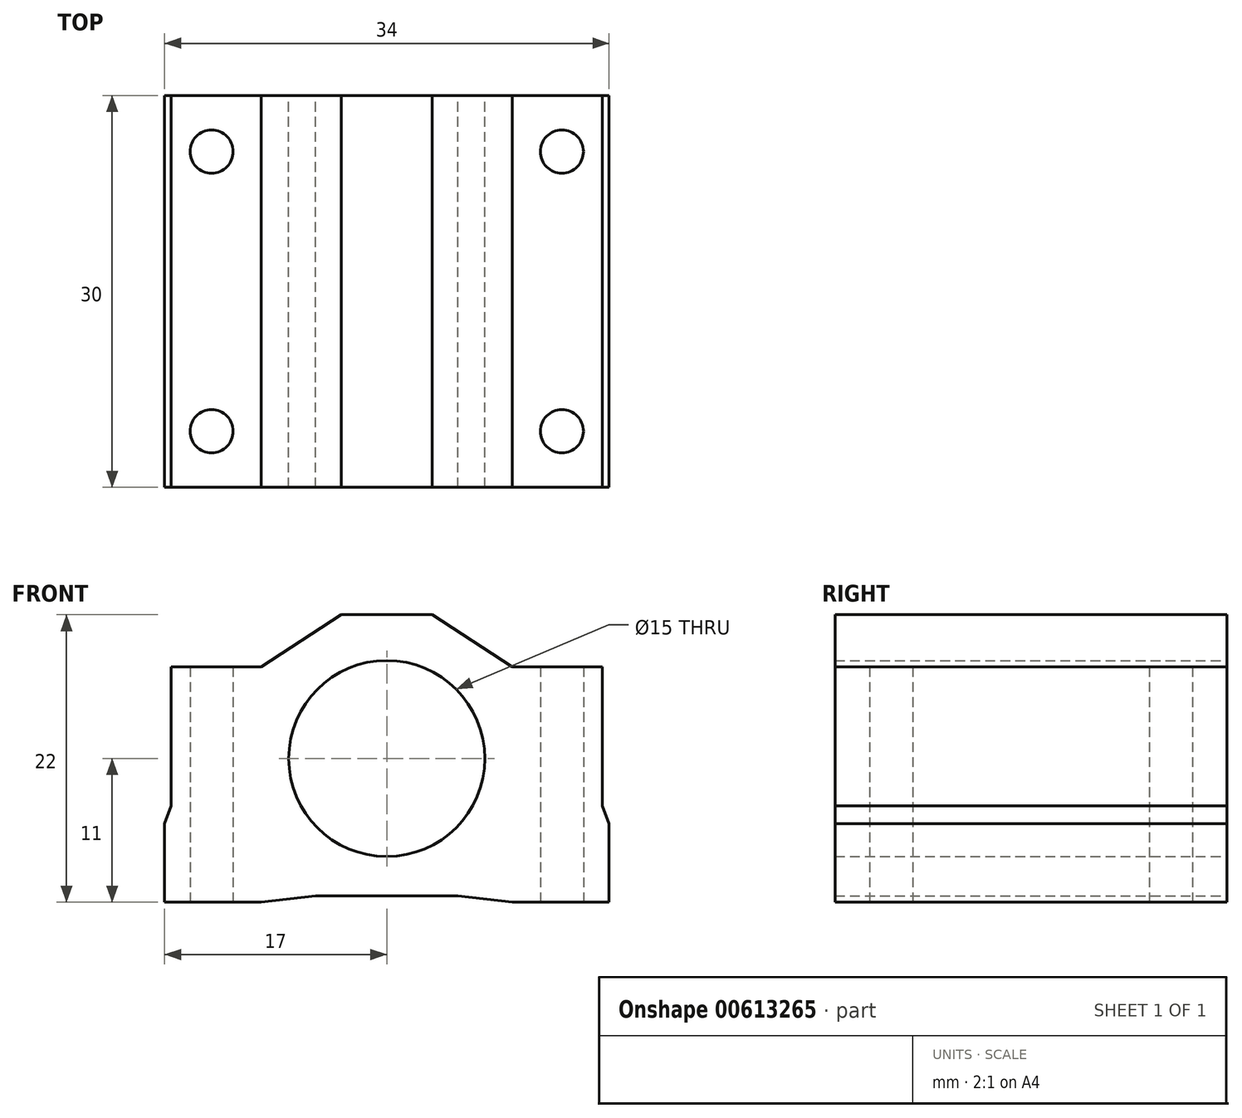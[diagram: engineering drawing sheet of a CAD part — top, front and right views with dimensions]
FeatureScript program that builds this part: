
annotation { "Feature Type Name" : "Feature", "Feature Type Description" : "" }
export const myFeature = defineFeature(function(context is Context, id is Id, definition is map)
    precondition{}
    {
        {
            var Q0;
            Q0=qCreatedBy(makeId("Front.planeOp"),FACE);
            var sketch = newSketch(context, id + "F0", { "sketchPlane" : qUnion([Q0])});
            skLineSegment(sketch, "E0", {"start": v(0, 0) * mm, "end": v(-5.45, 0) * mm});
            skLineSegment(sketch, "E1", {"start": v(-5.45, 0) * mm, "end": v(-9.61, -0.5) * mm});
            skLineSegment(sketch, "E2", {"start": v(-9.61, -0.5) * mm, "end": v(-17, -0.5) * mm});
            skLineSegment(sketch, "E3", {"start": v(-17, -0.5) * mm, "end": v(-17, 5.5) * mm});
            skLineSegment(sketch, "E4", {"start": v(-17, 5.5) * mm, "end": v(-16.5, 6.88) * mm});
            skLineSegment(sketch, "E5", {"start": v(-16.5, 6.88) * mm, "end": v(-16.5, 17.5) * mm});
            skLineSegment(sketch, "E6", {"start": v(-16.5, 17.5) * mm, "end": v(-9.61, 17.5) * mm});
            skLineSegment(sketch, "E7", {"start": v(-9.61, 17.5) * mm, "end": v(-3.48, 21.5) * mm});
            skLineSegment(sketch, "E8", {"start": v(-3.48, 21.5) * mm, "end": v(0, 21.5) * mm});
            skLineSegment(sketch, "E9", {"start": v(0, 21.5) * mm, "end": v(0, 0) * mm});
            skArc(sketch, "E10", {"start": v(0, 18) * mm, "mid": v(-7.5, 10.5) * mm, "end": v(0, 3) * mm});
            skLineSegment(sketch, "E11", {"start": v(-9.61, 28.72) * mm, "end": v(-9.61, -9.36) * mm, "construction": true});
            skLineSegment(sketch, "E12.MirrorCS", {"start": v(17, 5.5) * mm, "end": v(16.5, 6.88) * mm});
            skLineSegment(sketch, "E13.MirrorCS", {"start": v(0, 0) * mm, "end": v(5.45, 0) * mm});
            skLineSegment(sketch, "E14.MirrorCS", {"start": v(5.45, 0) * mm, "end": v(9.61, -0.5) * mm});
            skLineSegment(sketch, "E15.MirrorCS", {"start": v(9.61, -0.5) * mm, "end": v(17, -0.5) * mm});
            skLineSegment(sketch, "E16.MirrorCS", {"start": v(17, -0.5) * mm, "end": v(17, 5.5) * mm});
            skLineSegment(sketch, "E17.MirrorCS", {"start": v(16.5, 6.88) * mm, "end": v(16.5, 17.5) * mm});
            skLineSegment(sketch, "E18.MirrorCS", {"start": v(16.5, 17.5) * mm, "end": v(9.61, 17.5) * mm});
            skLineSegment(sketch, "E19.MirrorCS", {"start": v(9.61, 17.5) * mm, "end": v(3.48, 21.5) * mm});
            skLineSegment(sketch, "E20.MirrorCS", {"start": v(3.48, 21.5) * mm, "end": v(0, 21.5) * mm});
            skArc(sketch, "E21.MirrorCS", {"start": v(0, 18) * mm, "mid": v(7.5, 10.5) * mm, "end": v(0, 3) * mm});
            skSolve(sketch);
        }
        {
            var Q0;
            {var subQ2=sQuery(id+"F0.wireOp",EDGE,"E0");Q0=makeQuery(id+"F0.imprint","IMPRINT",FACE,{"disambiguationData":[TD([[makeQuery(id+"F0.imprint","IMPRINT",EDGE,{"derivedFrom":subQ2}),-1.0]])]});}
            var Q1;
            Q1=makeQuery(id+"F0.imprint","IMPRINT",FACE,{"disambiguationData":[TD([[makeQuery(id+"F0.imprint","IMPRINT",EDGE,{"derivedFrom":sQuery(id+"F0.wireOp",EDGE,"E12.MirrorCS")}),1.0]])]});
            extrude(context, id + "F1", {"entities" : qUnion([Q0, Q1]), "endBound" : BoundingType.SYMMETRIC, "depth" : 30 * mm, "offsetDistance" : 25 * mm});
        }
        {
            var Q0;
            Q0=makeQuery(id+"F1.opExtrude","SWEPT_FACE",FACE,{"disambiguationData":[OSD([sQuery(id+"F0.wireOp",EDGE,"E2")])]});
            var sketch = newSketch(context, id + "F2", { "sketchPlane" : qUnion([Q0])});
            skPoint(sketch, "E22", {"position": v(-13.4, 10.7) * mm});
            skPoint(sketch, "E23", {"position": v(-13.4, -10.7) * mm});
            skPoint(sketch, "E24.MirrorP", {"position": v(13.4, 10.7) * mm});
            skPoint(sketch, "E25.MirrorP", {"position": v(13.4, -10.7) * mm});
            skSolve(sketch);
        }
        {
            var Q0;
            Q0=sQuery(id+"F2.wireOp",VERTEX,"E22");
            var Q1;
            Q1=sQuery(id+"F2.wireOp",VERTEX,"E23");
            var Q2;
            Q2=sQuery(id+"F2.wireOp",VERTEX,"E25.MirrorP");
            var Q3;
            Q3=sQuery(id+"F2.wireOp",VERTEX,"E24.MirrorP");
            var Q4;
            Q4=makeQuery(id+"F1.opExtrude","SWEPT_BODY",BODY,{"disambiguationData":[OSD([sQuery(id+"F0.wireOp",EDGE,"E0"),sQuery(id+"F0.wireOp",EDGE,"E1"),sQuery(id+"F0.wireOp",EDGE,"E2"),sQuery(id+"F0.wireOp",EDGE,"E3"),sQuery(id+"F0.wireOp",EDGE,"E4"),sQuery(id+"F0.wireOp",EDGE,"E5"),sQuery(id+"F0.wireOp",EDGE,"E6"),sQuery(id+"F0.wireOp",EDGE,"E7"),sQuery(id+"F0.wireOp",EDGE,"E8"),sQuery(id+"F0.wireOp",EDGE,"E10"),sQuery(id+"F0.wireOp",EDGE,"E12.MirrorCS"),sQuery(id+"F0.wireOp",EDGE,"E13.MirrorCS"),sQuery(id+"F0.wireOp",EDGE,"E14.MirrorCS"),sQuery(id+"F0.wireOp",EDGE,"E15.MirrorCS"),sQuery(id+"F0.wireOp",EDGE,"E16.MirrorCS"),sQuery(id+"F0.wireOp",EDGE,"E17.MirrorCS"),sQuery(id+"F0.wireOp",EDGE,"E18.MirrorCS"),sQuery(id+"F0.wireOp",EDGE,"E19.MirrorCS"),sQuery(id+"F0.wireOp",EDGE,"E20.MirrorCS"),sQuery(id+"F0.wireOp",EDGE,"E21.MirrorCS")])]});
            hole(context, id + "F3", {"style" : HoleStyle.SIMPLE, "endStyle" : HoleEndStyle.THROUGH, "standardTappedOrClearance" : lookupTablePath({ "standard" : "ISO", "fit" : "Normal", "size" : "M3", "type" : "Clearance" }), "standardBlindInLast" : lookupTablePath({ "fit" : "Standard", "standard" : "ISO", "size" : "M3", "type" : "Clearance" }), "holeDiameter" : 3.3 * mm, "majorDiameter" : 5 * mm, "isTappedThrough" : true, "tappedDepth" : 12 * mm, "tapClearance" : 3, "locations" : qUnion([Q0, Q1, Q2, Q3]), "scope" : qUnion([Q4])});
        }
    });
